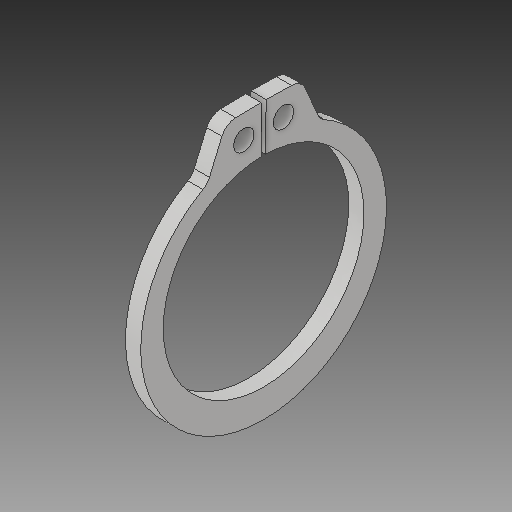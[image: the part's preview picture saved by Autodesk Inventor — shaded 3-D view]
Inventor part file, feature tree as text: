
AUTODESK INVENTOR PART (.ipt)
format: ipt  version: 2018 (Build 220112000, 112)  size: 102,912 bytes
history: native  units: in
note: dims shown in document units (in); Inventor stores cm internally (conversion verified against a paired STEP export)
features: fillet x1
ambient origin geometry x8: Origin, YZ Plane, XZ Plane, XY Plane, X Axis, Y Axis, Z Axis, Center Point
bodies: Solid1 (feature_tree)
feature tree (1):
  fillet  "Fillet1"  [1 undecoded]
note: 1 required parameter value undecoded (feature->parameter linkage not recoverable at this tier; creation-order binding heuristic only, values carry confidence <= 0.55)
